SOLIDWORKS PART (.sldprt)
format: sldprt  version: not decoded by parser v0  size: 289,792 bytes
history: native  units: mm
features: sketch x13, extrude x6, plane x4, sweep x2, revolve x2, material x1, helix x1, cut_extrude x1 (+10 scaffold rows collapsed)
feature tree (40):
  scaffold x10  (default folders/planes/origin — collapsed)
  material  "Matériau <non spécifié>"
  plane  "Plan1"
  plane  "Plan2"
  plane  "Plan3"
  sketch  "Esquisse1"  dims[Dt=10.49mm]
  extrude  "Base-Extrusion"  Depth=30mm
  sketch  "EsquisseR"  dims[D1=4.62mm]
  extrude  "RaccordD"  Depth=3.578mm
  sketch  "Esquisse8"  dims[D1=0.0mm]
  extrude  "RaccordG"  Depth=3.578mm
  sketch  "Construction"  dims[c1.Dp=3.75mm c1.D1=22.0mm c2.D1=~14.036243deg c2.ap=349.0mm c2.Dn=3.99mm c3.D1=1.99mm c3.D2=5.4548mm c3.Dp=2.43mm c3.px=3.98mm]
  sketch  "Esquisse3"  dims[Dn=7.98mm]
  helix  "Hélice1G"  Pitch=16.99mm
  sketch  "Esquisse5"  dims[D1=0.0mm]
  extrude  "Hélice1D"  Depth=16.99mm
  sketch  "Filet1G"
  sketch  "Filet1D"  dims[D1=0.0mm]
  sweep  "Enlèvement de matière-Balayage1"
  sweep  "Enlèvement de matière-Balayage2"
  sketch  "Esquisse9"
  cut_extrude  "Enlèv. mat.-Extru.2"  [1 undecoded]
  sketch  "Esquisse10"  dims[c1.D1=4.0mm c1.D2=2.5mm c1.D3=10.0mm c1.D4=6.0mm c2.D1=4.0mm c2.D4=6.0mm]
  revolve  "Révolution3"  [1 undecoded]
  plane  "Plan4"  Offset=50mm
  sketch  "Esquisse12"  dims[D1=10.0mm]
  extrude  "Extrusion1"  [1 undecoded]
  sketch  "Esquisse14"
  extrude  "Extrusion2"  Depth=30mm
  sketch  "Esquisse15"  dims[c1.D1=155.0mm c1.D2=32.0mm c1.D3=19.0mm c1.D4=15.0mm c1.D5=12.5mm c1.D6=8.0mm c1.D7=80.0mm c1.D8=140.0mm c1.D9=53.0mm c1.D10=7.5mm c1.D11=0.75mm c1.D12=7.0mm c2.D11=0.75mm c2.D1=12.0mm c2.D3=15.5mm c2.D5=9.5mm]
  revolve  "Révolution4"  [1 undecoded]
decode coverage: 16 of 25 modeling features carry decoded parameters
note: ~ marks probable driven/reference dimensions
note: 4 parameter values undecoded
summary: no parameter record found for 4 features
note: suppression state not decoded; provenance and decode notes live in map.json
